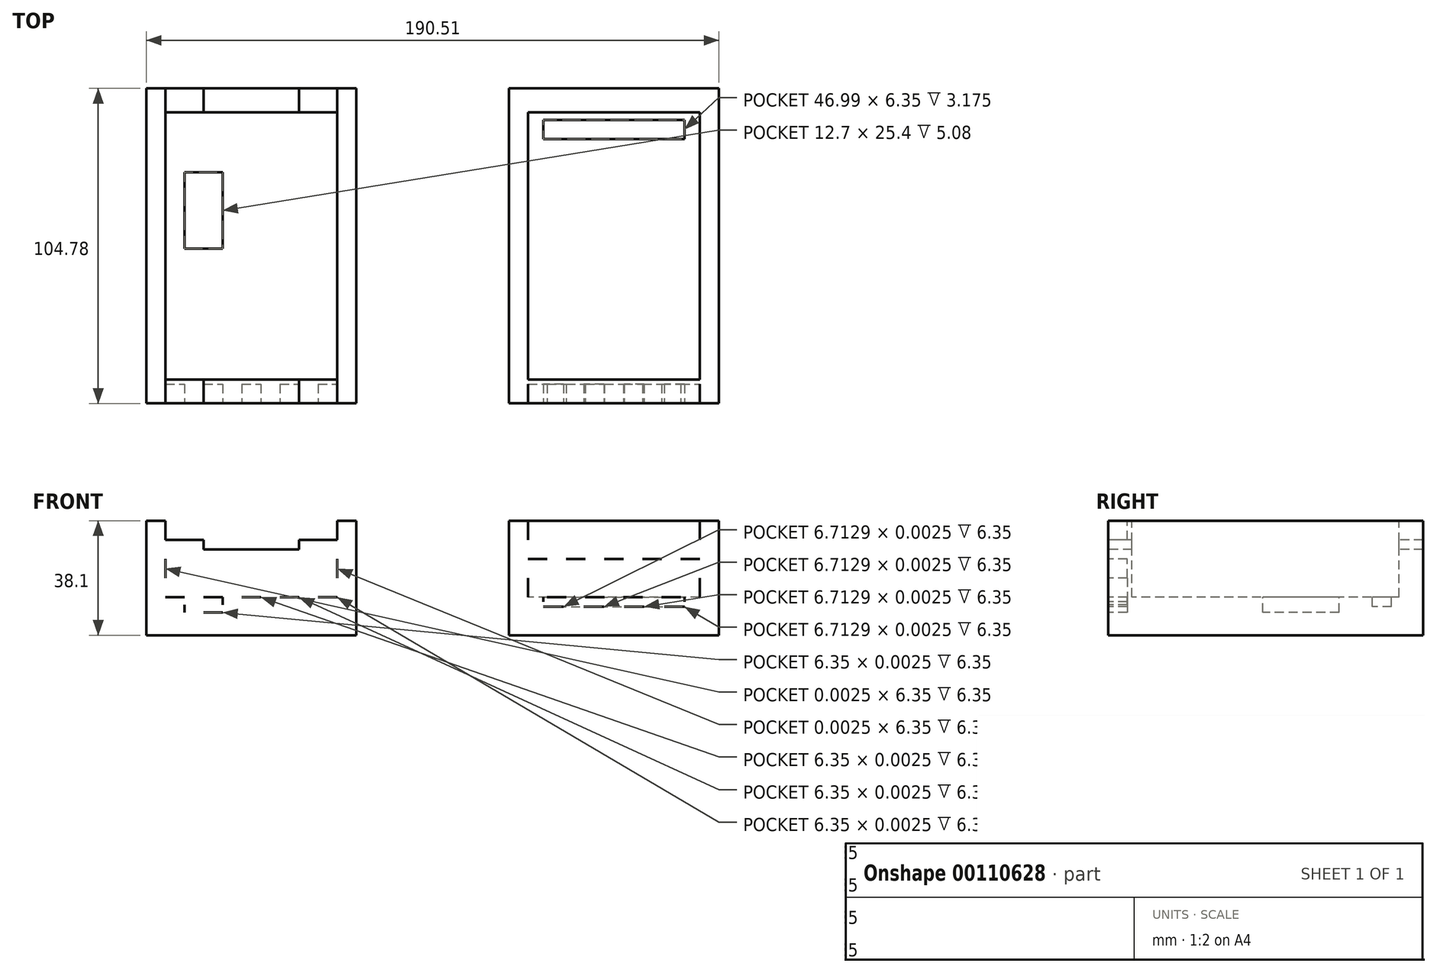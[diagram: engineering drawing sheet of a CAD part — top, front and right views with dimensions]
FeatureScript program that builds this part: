
annotation { "Feature Type Name" : "Feature", "Feature Type Description" : "" }
export const myFeature = defineFeature(function(context is Context, id is Id, definition is map)
    precondition{}
    {
        {
            var Q0;
            Q0=qCreatedBy(makeId("Top.planeOp"),FACE);
            var sketch = newSketch(context, id + "F0", { "sketchPlane" : qUnion([Q0])});
            skLineSegment(sketch, "E0.bottom", {"start": v(34.93, 52.39) * mm, "end": v(-34.92, 52.39) * mm});
            skLineSegment(sketch, "E0.top", {"start": v(34.93, -52.39) * mm, "end": v(-34.93, -52.39) * mm});
            skLineSegment(sketch, "E0.left", {"start": v(34.93, 52.39) * mm, "end": v(34.92, -52.39) * mm});
            skLineSegment(sketch, "E0.right", {"start": v(-34.92, 52.39) * mm, "end": v(-34.93, -52.39) * mm});
            skPoint(sketch, "E0.middle", {"position": v(0, 0) * mm});
            skLineSegment(sketch, "E1.bottom", {"start": v(-85.74, 52.39) * mm, "end": v(-155.6, 52.39) * mm});
            skLineSegment(sketch, "E1.top", {"start": v(-85.74, -52.39) * mm, "end": v(-155.6, -52.39) * mm});
            skLineSegment(sketch, "E1.left", {"start": v(-85.74, 52.39) * mm, "end": v(-85.74, -52.39) * mm});
            skLineSegment(sketch, "E1.right", {"start": v(-155.6, 52.39) * mm, "end": v(-155.6, -52.39) * mm});
            skPoint(sketch, "E1.middle", {"position": v(-120.67, 0) * mm});
            skSolve(sketch);
        }
        {
            var Q0;
            Q0 = qSketchRegion(id + "F0", true);
            extrude(context, id + "F1", {"entities" : qUnion([Q0]), "oppositeDirection" : true, "depth" : 38.1 * mm});
        }
        {
            var Q0;
            Q0=qCreatedBy(makeId("Top.planeOp"),FACE);
            var sketch = newSketch(context, id + "F2", { "sketchPlane" : qUnion([Q0])});
            skLineSegment(sketch, "E2.bottom", {"start": v(28.58, 44.45) * mm, "end": v(-28.58, 44.45) * mm});
            skLineSegment(sketch, "E2.top", {"start": v(28.58, -44.45) * mm, "end": v(-28.58, -44.45) * mm});
            skLineSegment(sketch, "E2.left", {"start": v(28.58, 44.45) * mm, "end": v(28.58, -44.45) * mm});
            skLineSegment(sketch, "E2.right", {"start": v(-28.58, 44.45) * mm, "end": v(-28.58, -44.45) * mm});
            skPoint(sketch, "E2.middle", {"position": v(0, 0) * mm});
            skLineSegment(sketch, "E3.bottom", {"start": v(-92.1, 44.45) * mm, "end": v(-149.24, 44.45) * mm});
            skLineSegment(sketch, "E3.top", {"start": v(-92.1, -44.45) * mm, "end": v(-149.24, -44.45) * mm});
            skLineSegment(sketch, "E3.left", {"start": v(-92.1, 44.45) * mm, "end": v(-92.1, -44.45) * mm});
            skLineSegment(sketch, "E3.right", {"start": v(-149.24, 44.45) * mm, "end": v(-149.24, -44.45) * mm});
            skPoint(sketch, "E3.middle", {"position": v(-120.67, 0) * mm});
            skPoint(sketch, "E3.middle.positionSnap0", {"position": v(-28.58, 0) * mm});
            skPoint(sketch, "E3.centerSnap0", {"position": v(-28.58, 0) * mm});
            skLineSegment(sketch, "E4", {"start": v(-92.1, 44.45) * mm, "end": v(-85.74, 44.45) * mm, "construction": true});
            skLineSegment(sketch, "E5", {"start": v(-149.24, 44.45) * mm, "end": v(-155.6, 44.45) * mm, "construction": true});
            skSolve(sketch);
        }
        {
            var Q0;
            Q0=makeQuery(id+"F2.imprint","IMPRINT",FACE,{"disambiguationData":[TD([[makeQuery(id+"F2.imprint","IMPRINT",EDGE,{"derivedFrom":sQuery(id+"F2.wireOp",EDGE,"E2.bottom")}),1.0]])]});
            var Q1;
            Q1=sQuery(id+"F2.wireOp",EDGE,"E3.right");
            var Q2;
            Q2=sQuery(id+"F2.wireOp",EDGE,"E3.bottom");
            var Q3;
            Q3=sQuery(id+"F2.wireOp",EDGE,"E3.left");
            var Q4;
            Q4=sQuery(id+"F2.wireOp",EDGE,"E3.top");
            var Q5;
            Q5=sQuery(id+"F2.wireOp",EDGE,"E2.bottom");
            var Q6;
            Q6=sQuery(id+"F2.wireOp",EDGE,"E2.right");
            var Q7;
            Q7=sQuery(id+"F2.wireOp",EDGE,"E2.left");
            var Q8;
            Q8=sQuery(id+"F2.wireOp",EDGE,"E2.top");
            extrude(context, id + "F3", {"entities" : qUnion([Q0]), "operationType" : NewBodyOperationType.REMOVE, "surfaceEntities" : qUnion([Q1, Q2, Q3, Q4, Q5, Q6, Q7, Q8]), "oppositeDirection" : true, "depth" : 25.4 * mm});
        }
        {
            var Q0;
            Q0=makeQuery(id+"F3.boolean.opBoolean","COPY",FACE,{"derivedFrom":makeQuery(id+"F3.opExtrude","CAP_FACE",FACE,{"disambiguationData":[OSD([sQuery(id+"F2.wireOp",EDGE,"E2.bottom"),sQuery(id+"F2.wireOp",EDGE,"E2.top"),sQuery(id+"F2.wireOp",EDGE,"E2.left"),sQuery(id+"F2.wireOp",EDGE,"E2.right")])],"isStart":false})});
            var sketch = newSketch(context, id + "F4", { "sketchPlane" : qUnion([Q0])});
            skLineSegment(sketch, "E6.bottom", {"start": v(-28.58, -44.45) * mm, "end": v(28.58, -44.45) * mm});
            skLineSegment(sketch, "E6.top", {"start": v(-28.58, -19.05) * mm, "end": v(28.58, -19.05) * mm});
            skLineSegment(sketch, "E6.left", {"start": v(-28.58, -44.45) * mm, "end": v(-28.58, -19.05) * mm});
            skLineSegment(sketch, "E6.right", {"start": v(28.58, -44.45) * mm, "end": v(28.58, -19.05) * mm});
            skSolve(sketch);
        }
        {
            var Q0;
            Q0 = qSketchRegion(id + "F4", true);
            extrude(context, id + "F5", {"entities" : qUnion([Q0]), "operationType" : NewBodyOperationType.ADD, "depth" : 12.7 * mm});
        }
        {
            var Q0;
            Q0 = qSketchRegion(id + "F2", true);
            extrude(context, id + "F6", {"entities" : qUnion([Q0]), "operationType" : NewBodyOperationType.REMOVE, "oppositeDirection" : true, "depth" : 25.4 * mm});
        }
        {
            var Q0;
            Q0=makeQuery(id+"F1.opExtrude","SWEPT_FACE",FACE,{"disambiguationData":[OSD([sQuery(id+"F0.wireOp",EDGE,"E1.top")])]});
            var sketch = newSketch(context, id + "F7", { "sketchPlane" : qUnion([Q0])});
            skLineSegment(sketch, "E7", {"start": v(-149.24, 0) * mm, "end": v(-149.24, -6.35) * mm});
            skLineSegment(sketch, "E8", {"start": v(-149.24, -6.35) * mm, "end": v(-136.54, -6.35) * mm});
            skLineSegment(sketch, "E9", {"start": v(-136.54, -6.35) * mm, "end": v(-136.54, -9.53) * mm});
            skLineSegment(sketch, "E10", {"start": v(-136.54, -9.53) * mm, "end": v(-104.8, -9.53) * mm});
            skLineSegment(sketch, "E11", {"start": v(-104.8, -9.53) * mm, "end": v(-104.8, -6.35) * mm});
            skLineSegment(sketch, "E12", {"start": v(-104.8, -6.35) * mm, "end": v(-92.1, -6.35) * mm});
            skLineSegment(sketch, "E13", {"start": v(-92.1, -6.35) * mm, "end": v(-92.1, 0) * mm});
            skLineSegment(sketch, "E14", {"start": v(-92.1, 0) * mm, "end": v(-149.24, 0) * mm});
            skSolve(sketch);
        }
        {
            var Q0;
            Q0 = qSketchRegion(id + "F7", true);
            extrude(context, id + "F8", {"entities" : qUnion([Q0]), "operationType" : NewBodyOperationType.REMOVE, "endBound" : BoundingType.THROUGH_ALL, "oppositeDirection" : true, "depth" : 25.4 * mm});
        }
        {
            var Q0;
            Q0=makeQuery(id+"F6.boolean.opBoolean","COPY",FACE,{"derivedFrom":makeQuery(id+"F6.opExtrude","CAP_FACE",FACE,{"disambiguationData":[OSD([sQuery(id+"F2.wireOp",EDGE,"E3.bottom"),sQuery(id+"F2.wireOp",EDGE,"E3.top"),sQuery(id+"F2.wireOp",EDGE,"E3.left"),sQuery(id+"F2.wireOp",EDGE,"E3.right")])],"isStart":false})});
            var sketch = newSketch(context, id + "F9", { "sketchPlane" : qUnion([Q0])});
            skLineSegment(sketch, "E15.bottom", {"start": v(-142.9, 24.45) * mm, "end": v(-130.2, 24.45) * mm});
            skLineSegment(sketch, "E15.top", {"start": v(-142.9, -0.95) * mm, "end": v(-130.2, -0.95) * mm});
            skLineSegment(sketch, "E15.left", {"start": v(-142.9, 24.45) * mm, "end": v(-142.9, -0.95) * mm});
            skLineSegment(sketch, "E15.right", {"start": v(-130.2, 24.45) * mm, "end": v(-130.2, -0.95) * mm});
            skSolve(sketch);
        }
        {
            var Q0;
            Q0 = qSketchRegion(id + "F9", true);
            extrude(context, id + "F10", {"entities" : qUnion([Q0]), "operationType" : NewBodyOperationType.REMOVE, "oppositeDirection" : true, "depth" : 5.08 * mm});
        }
        {
            var Q0;
            Q0=makeQuery(id+"F3.boolean.opBoolean","COPY",FACE,{"derivedFrom":makeQuery(id+"F3.opExtrude","CAP_FACE",FACE,{"disambiguationData":[OSD([sQuery(id+"F2.wireOp",EDGE,"E2.bottom"),sQuery(id+"F2.wireOp",EDGE,"E2.top"),sQuery(id+"F2.wireOp",EDGE,"E2.left"),sQuery(id+"F2.wireOp",EDGE,"E2.right")])],"isStart":false})});
            var sketch = newSketch(context, id + "F11", { "sketchPlane" : qUnion([Q0])});
            skLineSegment(sketch, "E16.bottom", {"start": v(-23.5, 41.91) * mm, "end": v(23.5, 41.91) * mm});
            skLineSegment(sketch, "E16.top", {"start": v(-23.5, 35.56) * mm, "end": v(23.5, 35.56) * mm});
            skLineSegment(sketch, "E16.left", {"start": v(-23.5, 41.91) * mm, "end": v(-23.5, 35.56) * mm});
            skLineSegment(sketch, "E16.right", {"start": v(23.5, 41.91) * mm, "end": v(23.5, 35.56) * mm});
            skPoint(sketch, "E17", {"position": v(0, 35.56) * mm});
            skSolve(sketch);
        }
        {
            var Q0;
            Q0 = qSketchRegion(id + "F11", true);
            extrude(context, id + "F12", {"entities" : qUnion([Q0]), "operationType" : NewBodyOperationType.REMOVE, "oppositeDirection" : true, "depth" : 3.17 * mm});
        }
        {
            var Q0;
            Q0=makeQuery(id+"F1.opExtrude","SWEPT_FACE",FACE,{"disambiguationData":[OSD([sQuery(id+"F0.wireOp",EDGE,"E0.top")])]});
            var sketch = newSketch(context, id + "F13", { "sketchPlane" : qUnion([Q0])});
            skPoint(sketch, "E18", {"position": v(-28.58, 0) * mm});
            skPoint(sketch, "E19", {"position": v(-28.58, -12.7) * mm});
            skPoint(sketch, "E20", {"position": v(-28.58, -25.4) * mm});
            skPoint(sketch, "E21", {"position": v(28.58, -25.4) * mm});
            skPoint(sketch, "E22", {"position": v(28.58, -12.7) * mm});
            skPoint(sketch, "E23", {"position": v(28.58, 0) * mm});
            skLineSegment(sketch, "E24", {"start": v(-28.58, -12.7) * mm, "end": v(-22.23, -12.7) * mm});
            skLineSegment(sketch, "E25", {"start": v(-22.23, -12.7) * mm, "end": v(-15.88, -12.7) * mm, "construction": true});
            skLineSegment(sketch, "E26", {"start": v(-15.88, -12.7) * mm, "end": v(-9.53, -12.7) * mm});
            skLineSegment(sketch, "E27", {"start": v(-9.53, -12.7) * mm, "end": v(-3.18, -12.7) * mm, "construction": true});
            skLineSegment(sketch, "E28", {"start": v(-3.18, -12.7) * mm, "end": v(3.18, -12.7) * mm});
            skLineSegment(sketch, "E29", {"start": v(3.18, -12.7) * mm, "end": v(9.53, -12.7) * mm, "construction": true});
            skLineSegment(sketch, "E30", {"start": v(9.53, -12.7) * mm, "end": v(15.88, -12.7) * mm});
            skLineSegment(sketch, "E31", {"start": v(15.88, -12.7) * mm, "end": v(22.23, -12.7) * mm, "construction": true});
            skLineSegment(sketch, "E32", {"start": v(22.23, -12.7) * mm, "end": v(28.58, -12.7) * mm});
            skLineSegment(sketch, "E33", {"start": v(-28.58, -12.7) * mm, "end": v(-28.58, -6.35) * mm, "construction": true});
            skLineSegment(sketch, "E34", {"start": v(-28.58, -6.35) * mm, "end": v(-28.58, 0) * mm});
            skLineSegment(sketch, "E35", {"start": v(-28.58, -12.7) * mm, "end": v(-28.58, -19.05) * mm, "construction": true});
            skLineSegment(sketch, "E36", {"start": v(-28.58, -19.05) * mm, "end": v(-28.58, -25.4) * mm});
            skLineSegment(sketch, "E37", {"start": v(28.58, -12.7) * mm, "end": v(28.58, -6.35) * mm, "construction": true});
            skLineSegment(sketch, "E38", {"start": v(28.58, -6.35) * mm, "end": v(28.58, 0) * mm});
            skLineSegment(sketch, "E39", {"start": v(28.58, -12.7) * mm, "end": v(28.58, -19.05) * mm, "construction": true});
            skLineSegment(sketch, "E40", {"start": v(28.58, -19.05) * mm, "end": v(28.58, -25.4) * mm});
            skLineSegment(sketch, "E41", {"start": v(-28.58, 0) * mm, "end": v(-28.57, 0) * mm});
            skLineSegment(sketch, "E42", {"start": v(-28.57, 0) * mm, "end": v(-28.57, -6.35) * mm});
            skLineSegment(sketch, "E43", {"start": v(-28.57, -6.35) * mm, "end": v(-28.58, -6.35) * mm});
            skLineSegment(sketch, "E44", {"start": v(-28.58, -19.05) * mm, "end": v(-28.57, -19.05) * mm});
            skLineSegment(sketch, "E45", {"start": v(-28.57, -19.05) * mm, "end": v(-28.57, -25.4) * mm});
            skLineSegment(sketch, "E46", {"start": v(-28.57, -25.4) * mm, "end": v(-28.58, -25.4) * mm});
            skLineSegment(sketch, "E47", {"start": v(-28.58, -12.7) * mm, "end": v(-28.58, -12.7) * mm});
            skLineSegment(sketch, "E48", {"start": v(-22.23, -12.7) * mm, "end": v(-22.23, -12.7) * mm});
            skLineSegment(sketch, "E49", {"start": v(-15.88, -12.7) * mm, "end": v(-15.88, -12.7) * mm});
            skLineSegment(sketch, "E50", {"start": v(-9.53, -12.7) * mm, "end": v(-9.53, -12.7) * mm});
            skLineSegment(sketch, "E51", {"start": v(-3.18, -12.7) * mm, "end": v(-3.18, -12.7) * mm});
            skLineSegment(sketch, "E52", {"start": v(3.18, -12.7) * mm, "end": v(3.18, -12.7) * mm});
            skLineSegment(sketch, "E53", {"start": v(9.53, -12.7) * mm, "end": v(9.53, -12.7) * mm});
            skLineSegment(sketch, "E54", {"start": v(15.88, -12.7) * mm, "end": v(15.88, -12.7) * mm});
            skLineSegment(sketch, "E55", {"start": v(22.23, -12.7) * mm, "end": v(22.23, -12.7) * mm});
            skLineSegment(sketch, "E56", {"start": v(28.58, -12.7) * mm, "end": v(28.58, -12.7) * mm});
            skLineSegment(sketch, "E57", {"start": v(28.58, -6.35) * mm, "end": v(28.57, -6.35) * mm});
            skLineSegment(sketch, "E58", {"start": v(28.57, -6.35) * mm, "end": v(28.57, 0) * mm});
            skLineSegment(sketch, "E59", {"start": v(28.57, 0) * mm, "end": v(28.58, 0) * mm});
            skLineSegment(sketch, "E60", {"start": v(28.58, -19.05) * mm, "end": v(28.57, -19.05) * mm});
            skLineSegment(sketch, "E61", {"start": v(28.57, -19.05) * mm, "end": v(28.57, -25.4) * mm});
            skLineSegment(sketch, "E62", {"start": v(28.57, -25.4) * mm, "end": v(28.58, -25.4) * mm});
            skLineSegment(sketch, "E63", {"start": v(-28.58, -25.4) * mm, "end": v(-22.23, -25.4) * mm, "construction": true});
            skLineSegment(sketch, "E64", {"start": v(-22.23, -25.4) * mm, "end": v(-15.88, -25.4) * mm});
            skLineSegment(sketch, "E65", {"start": v(-15.88, -25.4) * mm, "end": v(-9.53, -25.4) * mm, "construction": true});
            skLineSegment(sketch, "E66", {"start": v(-9.53, -25.4) * mm, "end": v(-3.18, -25.4) * mm});
            skLineSegment(sketch, "E67", {"start": v(-3.18, -25.4) * mm, "end": v(3.18, -25.4) * mm, "construction": true});
            skLineSegment(sketch, "E68", {"start": v(3.18, -25.4) * mm, "end": v(9.53, -25.4) * mm});
            skLineSegment(sketch, "E69", {"start": v(9.53, -25.4) * mm, "end": v(15.88, -25.4) * mm, "construction": true});
            skLineSegment(sketch, "E70", {"start": v(15.88, -25.4) * mm, "end": v(22.23, -25.4) * mm});
            skLineSegment(sketch, "E71", {"start": v(22.23, -25.4) * mm, "end": v(28.58, -25.4) * mm, "construction": true});
            skLineSegment(sketch, "E72", {"start": v(-22.23, -25.4) * mm, "end": v(-22.23, -25.4) * mm});
            skLineSegment(sketch, "E73", {"start": v(-15.88, -25.4) * mm, "end": v(-15.88, -25.4) * mm});
            skLineSegment(sketch, "E74", {"start": v(-9.53, -25.4) * mm, "end": v(-9.53, -25.4) * mm});
            skLineSegment(sketch, "E75", {"start": v(-3.18, -25.4) * mm, "end": v(-3.18, -25.4) * mm});
            skLineSegment(sketch, "E76", {"start": v(3.18, -25.4) * mm, "end": v(3.18, -25.4) * mm});
            skLineSegment(sketch, "E77", {"start": v(9.53, -25.4) * mm, "end": v(9.53, -25.4) * mm});
            skLineSegment(sketch, "E78", {"start": v(15.88, -25.4) * mm, "end": v(15.88, -25.4) * mm});
            skLineSegment(sketch, "E79", {"start": v(22.23, -25.4) * mm, "end": v(22.23, -25.4) * mm});
            skPoint(sketch, "E80", {"position": v(-23.5, -28.58) * mm});
            skPoint(sketch, "E81", {"position": v(23.5, -28.58) * mm});
            skLineSegment(sketch, "E82", {"start": v(-23.5, -28.58) * mm, "end": v(-23.5, -26.99) * mm, "construction": true});
            skLineSegment(sketch, "E83", {"start": v(-23.5, -26.99) * mm, "end": v(-23.5, -25.4) * mm});
            skLineSegment(sketch, "E84", {"start": v(23.5, -28.58) * mm, "end": v(23.5, -26.99) * mm, "construction": true});
            skLineSegment(sketch, "E85", {"start": v(23.5, -26.99) * mm, "end": v(23.5, -25.4) * mm});
            skLineSegment(sketch, "E86", {"start": v(23.5, -28.58) * mm, "end": v(16.78, -28.58) * mm});
            skLineSegment(sketch, "E87", {"start": v(16.78, -28.58) * mm, "end": v(10.07, -28.58) * mm, "construction": true});
            skLineSegment(sketch, "E88", {"start": v(10.07, -28.58) * mm, "end": v(3.36, -28.58) * mm});
            skLineSegment(sketch, "E89", {"start": v(3.36, -28.58) * mm, "end": v(-3.36, -28.58) * mm, "construction": true});
            skLineSegment(sketch, "E90", {"start": v(-3.36, -28.58) * mm, "end": v(-10.07, -28.58) * mm});
            skLineSegment(sketch, "E91", {"start": v(-10.07, -28.58) * mm, "end": v(-16.78, -28.58) * mm, "construction": true});
            skLineSegment(sketch, "E92", {"start": v(-16.78, -28.58) * mm, "end": v(-23.5, -28.58) * mm});
            skLineSegment(sketch, "E93", {"start": v(-23.5, -25.4) * mm, "end": v(-23.5, -25.4) * mm});
            skLineSegment(sketch, "E94", {"start": v(-23.5, -25.4) * mm, "end": v(-23.5, -26.99) * mm});
            skLineSegment(sketch, "E95", {"start": v(-23.5, -26.99) * mm, "end": v(-23.5, -26.99) * mm});
            skLineSegment(sketch, "E96", {"start": v(-23.5, -28.58) * mm, "end": v(-23.5, -28.58) * mm});
            skLineSegment(sketch, "E97", {"start": v(-23.5, -28.58) * mm, "end": v(-16.78, -28.58) * mm});
            skLineSegment(sketch, "E98", {"start": v(-16.78, -28.58) * mm, "end": v(-16.78, -28.58) * mm});
            skLineSegment(sketch, "E99", {"start": v(-10.07, -28.58) * mm, "end": v(-10.07, -28.58) * mm});
            skLineSegment(sketch, "E100", {"start": v(-10.07, -28.58) * mm, "end": v(-3.36, -28.58) * mm});
            skLineSegment(sketch, "E101", {"start": v(-3.36, -28.58) * mm, "end": v(-3.36, -28.58) * mm});
            skLineSegment(sketch, "E102", {"start": v(3.36, -28.58) * mm, "end": v(3.36, -28.58) * mm});
            skLineSegment(sketch, "E103", {"start": v(3.36, -28.58) * mm, "end": v(10.07, -28.58) * mm});
            skLineSegment(sketch, "E104", {"start": v(10.07, -28.58) * mm, "end": v(10.07, -28.58) * mm});
            skLineSegment(sketch, "E105", {"start": v(16.78, -28.58) * mm, "end": v(16.78, -28.58) * mm});
            skLineSegment(sketch, "E106", {"start": v(16.78, -28.58) * mm, "end": v(23.5, -28.58) * mm});
            skLineSegment(sketch, "E107", {"start": v(23.5, -28.58) * mm, "end": v(23.5, -28.58) * mm});
            skLineSegment(sketch, "E108", {"start": v(23.5, -25.4) * mm, "end": v(23.5, -25.4) * mm});
            skLineSegment(sketch, "E109", {"start": v(23.5, -25.4) * mm, "end": v(23.5, -26.99) * mm});
            skLineSegment(sketch, "E110", {"start": v(23.5, -26.99) * mm, "end": v(23.5, -26.99) * mm});
            skSolve(sketch);
        }
        {
            var Q0;
            Q0 = qSketchRegion(id + "F13", true);
            extrude(context, id + "F14", {"entities" : qUnion([Q0]), "operationType" : NewBodyOperationType.REMOVE, "oppositeDirection" : true, "depth" : 6.35 * mm});
        }
        {
            var Q0;
            Q0=makeQuery(id+"F1.opExtrude","SWEPT_FACE",FACE,{"disambiguationData":[OSD([sQuery(id+"F0.wireOp",EDGE,"E1.top")])]});
            var sketch = newSketch(context, id + "F15", { "sketchPlane" : qUnion([Q0])});
            skPoint(sketch, "E111", {"position": v(-142.9, -25.4) * mm});
            skPoint(sketch, "E112", {"position": v(-130.2, -25.4) * mm});
            skPoint(sketch, "E113", {"position": v(-142.9, -30.48) * mm});
            skPoint(sketch, "E114", {"position": v(-130.2, -30.48) * mm});
            skPoint(sketch, "E115", {"position": v(-149.24, -25.4) * mm});
            skPoint(sketch, "E116", {"position": v(-92.1, -25.4) * mm});
            skLineSegment(sketch, "E117", {"start": v(-149.24, -25.4) * mm, "end": v(-142.9, -25.4) * mm});
            skLineSegment(sketch, "E118", {"start": v(-142.9, -25.4) * mm, "end": v(-136.54, -25.4) * mm, "construction": true});
            skLineSegment(sketch, "E119", {"start": v(-136.54, -25.4) * mm, "end": v(-130.2, -25.4) * mm});
            skLineSegment(sketch, "E120", {"start": v(-130.2, -25.4) * mm, "end": v(-123.84, -25.4) * mm, "construction": true});
            skLineSegment(sketch, "E121", {"start": v(-123.84, -25.4) * mm, "end": v(-117.5, -25.4) * mm});
            skLineSegment(sketch, "E122", {"start": v(-117.5, -25.4) * mm, "end": v(-111.14, -25.4) * mm, "construction": true});
            skLineSegment(sketch, "E123", {"start": v(-111.14, -25.4) * mm, "end": v(-104.8, -25.4) * mm});
            skLineSegment(sketch, "E124", {"start": v(-104.8, -25.4) * mm, "end": v(-98.44, -25.4) * mm, "construction": true});
            skLineSegment(sketch, "E125", {"start": v(-98.44, -25.4) * mm, "end": v(-92.1, -25.4) * mm});
            skLineSegment(sketch, "E126", {"start": v(-142.9, -25.4) * mm, "end": v(-142.9, -27.94) * mm, "construction": true});
            skLineSegment(sketch, "E127", {"start": v(-142.9, -27.94) * mm, "end": v(-142.9, -30.48) * mm});
            skLineSegment(sketch, "E128", {"start": v(-130.2, -25.4) * mm, "end": v(-130.2, -27.94) * mm});
            skLineSegment(sketch, "E129", {"start": v(-130.2, -27.94) * mm, "end": v(-130.2, -30.48) * mm, "construction": true});
            skLineSegment(sketch, "E130", {"start": v(-142.9, -30.48) * mm, "end": v(-136.54, -30.48) * mm, "construction": true});
            skLineSegment(sketch, "E131", {"start": v(-136.54, -30.48) * mm, "end": v(-130.2, -30.48) * mm});
            skLineSegment(sketch, "E132", {"start": v(-149.24, -25.4) * mm, "end": v(-149.24, -19.05) * mm, "construction": true});
            skLineSegment(sketch, "E133", {"start": v(-149.24, -19.05) * mm, "end": v(-149.24, -12.7) * mm});
            skLineSegment(sketch, "E134", {"start": v(-149.24, -12.7) * mm, "end": v(-149.24, -6.35) * mm, "construction": true});
            skLineSegment(sketch, "E135", {"start": v(-92.1, -6.35) * mm, "end": v(-92.1, -12.7) * mm, "construction": true});
            skLineSegment(sketch, "E136", {"start": v(-92.1, -12.7) * mm, "end": v(-92.1, -19.05) * mm});
            skLineSegment(sketch, "E137", {"start": v(-92.1, -19.05) * mm, "end": v(-92.1, -25.4) * mm, "construction": true});
            skLineSegment(sketch, "E138", {"start": v(-149.24, -12.7) * mm, "end": v(-149.24, -12.7) * mm});
            skLineSegment(sketch, "E139", {"start": v(-149.24, -12.7) * mm, "end": v(-149.24, -19.05) * mm});
            skLineSegment(sketch, "E140", {"start": v(-149.24, -19.05) * mm, "end": v(-149.24, -19.05) * mm});
            skLineSegment(sketch, "E141", {"start": v(-149.24, -25.4) * mm, "end": v(-149.24, -25.4) * mm});
            skLineSegment(sketch, "E142", {"start": v(-142.9, -25.4) * mm, "end": v(-142.9, -25.4) * mm});
            skLineSegment(sketch, "E143", {"start": v(-136.54, -25.4) * mm, "end": v(-136.54, -25.4) * mm});
            skLineSegment(sketch, "E144", {"start": v(-130.2, -25.4) * mm, "end": v(-130.2, -25.4) * mm});
            skLineSegment(sketch, "E145", {"start": v(-123.84, -25.4) * mm, "end": v(-123.84, -25.4) * mm});
            skLineSegment(sketch, "E146", {"start": v(-117.5, -25.4) * mm, "end": v(-117.5, -25.4) * mm});
            skLineSegment(sketch, "E147", {"start": v(-111.14, -25.4) * mm, "end": v(-111.14, -25.4) * mm});
            skLineSegment(sketch, "E148", {"start": v(-104.8, -25.4) * mm, "end": v(-104.8, -25.4) * mm});
            skLineSegment(sketch, "E149", {"start": v(-98.44, -25.4) * mm, "end": v(-98.44, -25.4) * mm});
            skLineSegment(sketch, "E150", {"start": v(-92.1, -25.4) * mm, "end": v(-92.1, -25.4) * mm});
            skLineSegment(sketch, "E151", {"start": v(-92.1, -19.05) * mm, "end": v(-92.1, -19.05) * mm});
            skLineSegment(sketch, "E152", {"start": v(-92.1, -19.05) * mm, "end": v(-92.1, -12.7) * mm});
            skLineSegment(sketch, "E153", {"start": v(-92.1, -12.7) * mm, "end": v(-92.1, -12.7) * mm});
            skLineSegment(sketch, "E154", {"start": v(-142.9, -27.94) * mm, "end": v(-142.89, -27.94) * mm});
            skLineSegment(sketch, "E155", {"start": v(-142.89, -27.94) * mm, "end": v(-142.89, -30.48) * mm});
            skLineSegment(sketch, "E156", {"start": v(-142.89, -30.48) * mm, "end": v(-142.9, -30.48) * mm});
            skLineSegment(sketch, "E157", {"start": v(-136.54, -30.48) * mm, "end": v(-136.54, -30.48) * mm});
            skLineSegment(sketch, "E158", {"start": v(-130.2, -30.48) * mm, "end": v(-130.2, -30.48) * mm});
            skLineSegment(sketch, "E159", {"start": v(-130.2, -27.94) * mm, "end": v(-130.2, -27.94) * mm});
            skLineSegment(sketch, "E160", {"start": v(-130.2, -27.94) * mm, "end": v(-130.2, -25.4) * mm});
            skSolve(sketch);
        }
        {
            var Q0;
            Q0 = qSketchRegion(id + "F15", true);
            extrude(context, id + "F16", {"entities" : qUnion([Q0]), "operationType" : NewBodyOperationType.REMOVE, "oppositeDirection" : true, "depth" : 6.35 * mm});
        }
        {
            var Q0;
            Q0 = qSketchRegion(id + "F13", true);
            extrude(context, id + "F17", {"entities" : qUnion([Q0]), "operationType" : NewBodyOperationType.REMOVE, "oppositeDirection" : true, "depth" : 6.35 * mm});
        }
    });
